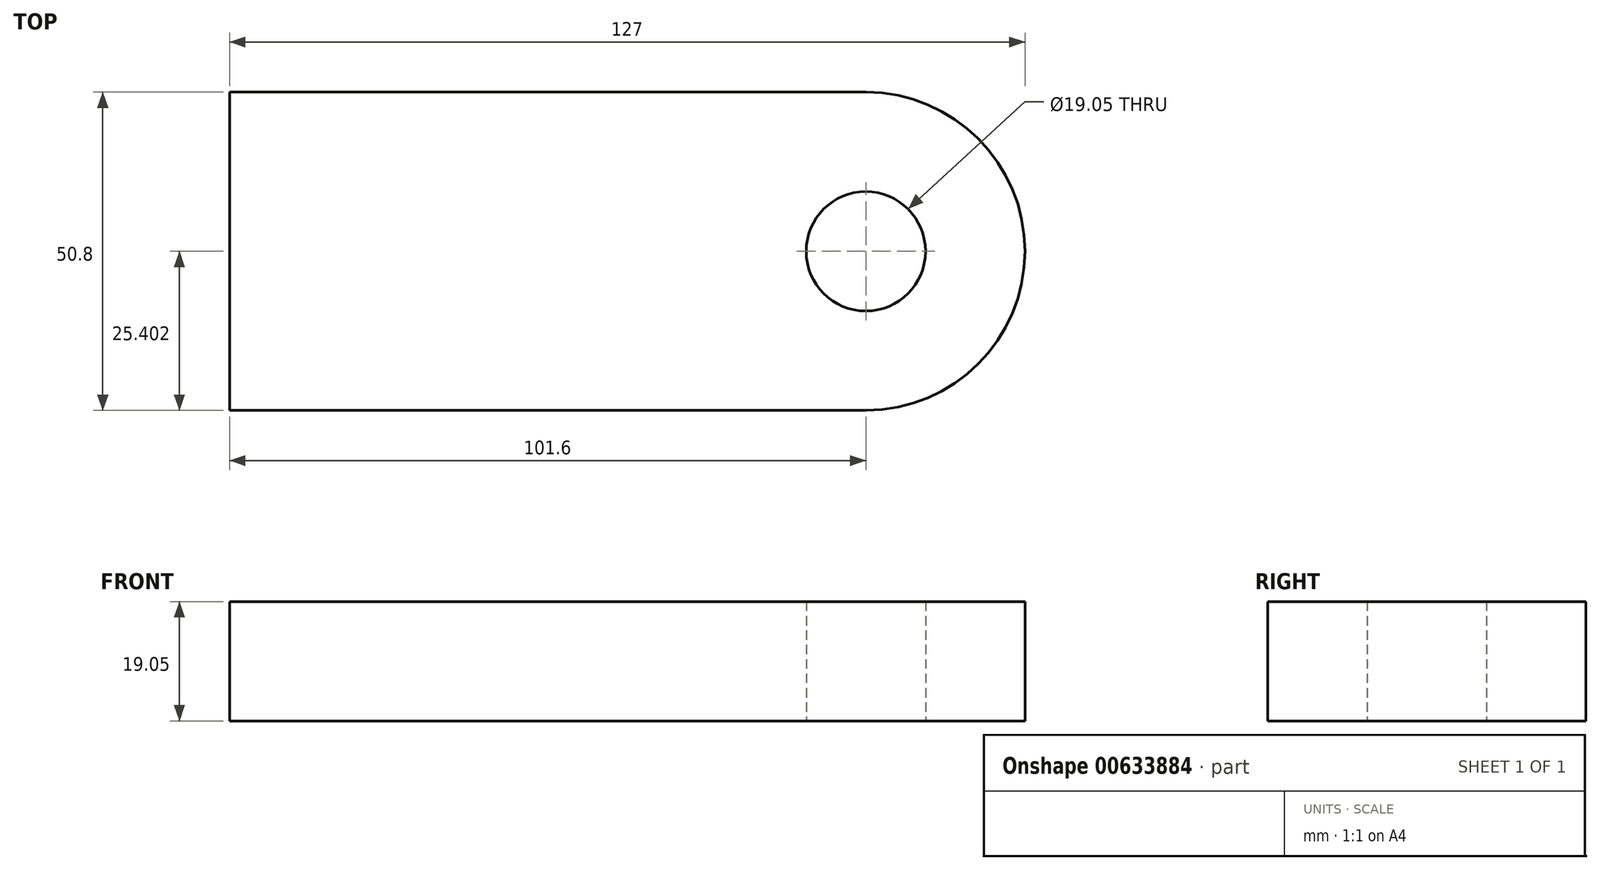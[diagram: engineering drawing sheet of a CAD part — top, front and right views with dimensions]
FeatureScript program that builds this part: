
annotation { "Feature Type Name" : "Feature", "Feature Type Description" : "" }
export const myFeature = defineFeature(function(context is Context, id is Id, definition is map)
    precondition{}
    {
        {
            var Q0;
            Q0=qCreatedBy(makeId("Top.planeOp"),FACE);
            var sketch = newSketch(context, id + "F0", { "sketchPlane" : qUnion([Q0])});
            skLineSegment(sketch, "E0.bottom", {"start": v(-101.6, -75.74) * mm, "end": v(0, -75.74) * mm});
            skLineSegment(sketch, "E0.top", {"start": v(-101.6, -24.94) * mm, "end": v(0, -24.94) * mm});
            skLineSegment(sketch, "E0.left", {"start": v(-101.6, -75.74) * mm, "end": v(-101.6, -24.94) * mm});
            skArc(sketch, "E1", {"start": v(0, -75.74) * mm, "mid": v(25.4, -50.34) * mm, "end": v(0, -24.94) * mm});
            skCircle(sketch, "E2", {"center": v(0, -50.34) * mm, "radius": 9.53 * mm});
            skSolve(sketch);
        }
        {
            var Q0;
            Q0=makeQuery(id+"F0.imprint","IMPRINT",FACE,{"disambiguationData":[TD([[makeQuery(id+"F0.imprint","IMPRINT",EDGE,{"derivedFrom":sQuery(id+"F0.wireOp",EDGE,"E0.bottom")}),1.0]])]});
            extrude(context, id + "F1", {"entities" : qUnion([Q0]), "depth" : 19.05 * mm, "offsetDistance" : 25.4 * mm});
        }
    });
